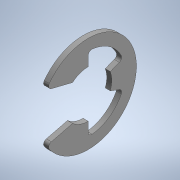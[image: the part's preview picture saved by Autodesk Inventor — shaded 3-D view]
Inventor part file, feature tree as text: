
AUTODESK INVENTOR PART (.ipt)
format: ipt  version: 2020 (Build 240168000, 168)  size: 100,864 bytes
history: native  units: mm (DEFAULTED — no unit token found)
features: fillet x1
ambient origin geometry x8: Origin, YZ Plane, XZ Plane, XY Plane, X Axis, Y Axis, Z Axis, Center Point
bodies: Solid1 (feature_tree)
feature tree (1):
  fillet  "Fillet1"  [1 undecoded]
note: 1 required parameter value undecoded (feature->parameter linkage not recoverable at this tier; creation-order binding heuristic only, values carry confidence <= 0.55)
